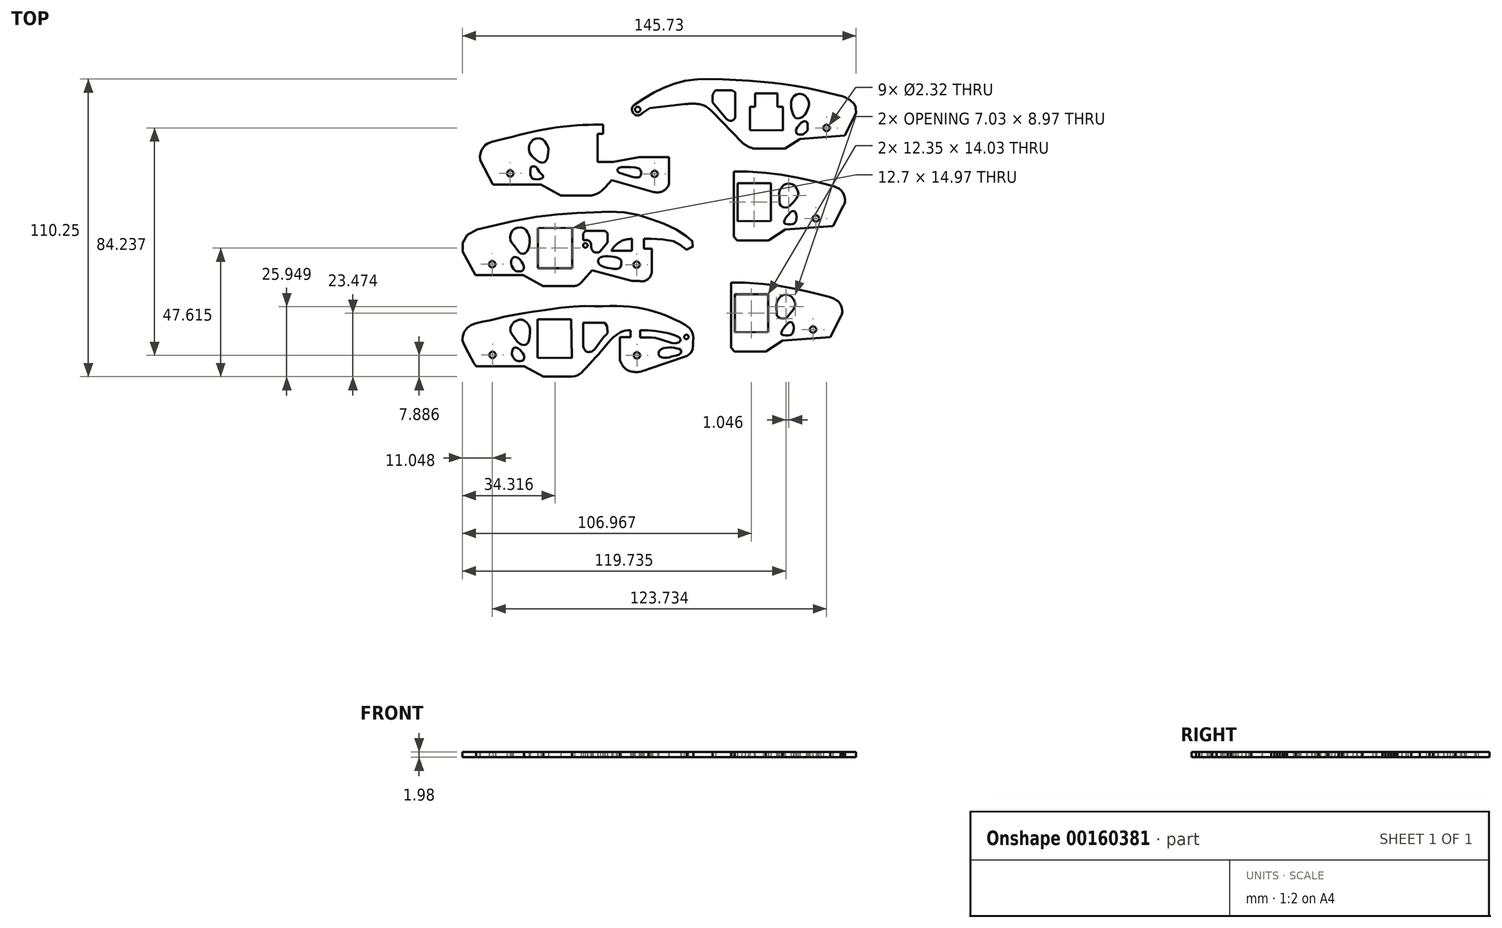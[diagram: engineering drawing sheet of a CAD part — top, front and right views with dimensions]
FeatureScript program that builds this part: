
annotation { "Feature Type Name" : "Feature", "Feature Type Description" : "" }
export const myFeature = defineFeature(function(context is Context, id is Id, definition is map)
    precondition{}
    {
        {
            var Q0;
            Q0=qCreatedBy(makeId("Top.planeOp"),FACE);
            var sketch = newSketch(context, id + "F0", { "sketchPlane" : qUnion([Q0])});
            skLineSegment(sketch, "E0", {"start": v(102.72, 106.46) * mm, "end": v(113.6, 95.26) * mm});
            skLineSegment(sketch, "E1", {"start": v(155.9, 105.94) * mm, "end": v(151.6, 97.67) * mm});
            skLineSegment(sketch, "E2", {"start": v(151.6, 97.67) * mm, "end": v(135.17, 96.41) * mm});
            skLineSegment(sketch, "E3", {"start": v(135.17, 96.41) * mm, "end": v(129.52, 92.85) * mm});
            skLineSegment(sketch, "E4", {"start": v(129.52, 92.85) * mm, "end": v(118.1, 92.85) * mm});
            skLineSegment(sketch, "E5", {"start": v(79.59, 107.92) * mm, "end": v(92.64, 109.39) * mm});
            skFitSpline(sketch, "E6", {"points": [v(76.87, 106.15) * mm, v(75.51, 105.3) * mm, v(74.14, 105.41) * mm, v(73, 106.88) * mm, v(73.1, 108.24) * mm, v(74.04, 109.29) * mm], "startDerivative": vector(-5.69, -6.58) * mm, "endDerivative": vector(5.78, 5.04) * mm});
            skPoint(sketch, "E7.10.internal.snap0", {"position": v(86.11, 108.66) * mm});
            skFitSpline(sketch, "E7", {"points": [v(74.04, 109.29) * mm, v(82.52, 114.41) * mm, v(92.64, 117.97) * mm, v(105.34, 118.6) * mm, v(118.84, 117.87) * mm, v(129.73, 116.72) * mm, v(140.61, 114.73) * mm, v(148.25, 112.84) * mm, v(152.55, 111.59) * mm, v(155.16, 109.39) * mm, v(155.57, 108.66) * mm, v(155.9, 105.94) * mm], "startDerivative": vector(74.24, 51.65) * mm, "endDerivative": vector(-2.1, -59) * mm});
            skFitSpline(sketch, "E8", {"points": [v(92.64, 109.39) * mm, v(97.7, 109.39) * mm, v(100.84, 108.13) * mm, v(102.72, 106.46) * mm], "startDerivative": vector(9.18, 0.98) * mm, "endDerivative": vector(5.58, -5.6) * mm});
            skFitSpline(sketch, "E9", {"points": [v(113.6, 95.26) * mm, v(115.5, 93.9) * mm, v(118.1, 92.85) * mm], "startDerivative": vector(3.71, -3.06) * mm, "endDerivative": vector(5.26, -1.77) * mm});
            skLineSegment(sketch, "E10", {"start": v(76.87, 106.15) * mm, "end": v(79.59, 107.92) * mm});
            skLineSegment(sketch, "E11", {"start": v(111.2, 105) * mm, "end": v(111.2, 113.68) * mm});
            skLineSegment(sketch, "E12", {"start": v(103.87, 114.52) * mm, "end": v(109.94, 114.52) * mm});
            skLineSegment(sketch, "E13", {"start": v(109.94, 114.52) * mm, "end": v(111.2, 113.68) * mm});
            skLineSegment(sketch, "E14", {"start": v(102.83, 110.02) * mm, "end": v(107.75, 104.05) * mm});
            skArc(sketch, "E15", {"start": v(107.75, 104.05) * mm, "mid": v(108.68, 103.37) * mm, "end": v(109.84, 103.21) * mm});
            skArc(sketch, "E16", {"start": v(111.2, 105) * mm, "mid": v(110.82, 103.87) * mm, "end": v(109.84, 103.21) * mm});
            skFitSpline(sketch, "E17", {"points": [v(102.83, 110.02) * mm, v(102.83, 112.74) * mm, v(103.87, 114.52) * mm], "startDerivative": vector(-0.6, 5.43) * mm, "endDerivative": vector(2.77, 3.53) * mm});
            skPoint(sketch, "E18.0.internal.snap0", {"position": v(105.29, 107.04) * mm});
            skFitSpline(sketch, "E18", {"points": [v(132.13, 107.04) * mm, v(131.82, 109.8) * mm, v(133.18, 112.64) * mm, v(136.32, 112.95) * mm, v(138, 111.17) * mm, v(138.41, 109.18) * mm, v(136.95, 105.55) * mm, v(134.65, 104.05) * mm, v(133.18, 104.47) * mm, v(132.13, 107.04) * mm]});
            skFitSpline(sketch, "E19", {"points": [v(133.8, 100.16) * mm, v(134.89, 101.65) * mm, v(135.97, 102.73) * mm, v(136.8, 103.02) * mm, v(137.84, 102.44) * mm, v(137.92, 100.9) * mm, v(137.88, 99.7) * mm, v(137.05, 98.79) * mm, v(136.26, 98.16) * mm, v(134.68, 98.12) * mm, v(134.02, 98.41) * mm, v(133.73, 98.91) * mm, v(133.8, 100.16) * mm]});
            skLineSegment(sketch, "E20", {"start": v(116.6, 99.72) * mm, "end": v(116.6, 108.38) * mm});
            skLineSegment(sketch, "E21", {"start": v(116.6, 108.38) * mm, "end": v(118.53, 108.38) * mm});
            skLineSegment(sketch, "E22", {"start": v(118.53, 108.38) * mm, "end": v(118.53, 113.41) * mm});
            skLineSegment(sketch, "E23", {"start": v(118.53, 113.41) * mm, "end": v(126.77, 113.41) * mm});
            skLineSegment(sketch, "E24", {"start": v(126.77, 113.41) * mm, "end": v(126.77, 108.42) * mm});
            skLineSegment(sketch, "E25", {"start": v(126.77, 108.42) * mm, "end": v(128.76, 108.42) * mm});
            skLineSegment(sketch, "E26", {"start": v(128.76, 108.42) * mm, "end": v(128.76, 99.68) * mm});
            skLineSegment(sketch, "E27", {"start": v(128.76, 99.68) * mm, "end": v(116.6, 99.72) * mm});
            skCircle(sketch, "E28", {"center": v(144.95, 100.53) * mm, "radius": 1.16 * mm});
            skCircle(sketch, "E29", {"center": v(75.05, 107.38) * mm, "radius": 1 * mm});
            skCircle(sketch, "E30", {"center": v(141, 67.03) * mm, "radius": 1.16 * mm});
            skLineSegment(sketch, "E31", {"start": v(110.65, 84.35) * mm, "end": v(110.65, 60.33) * mm});
            skLineSegment(sketch, "E32", {"start": v(110.65, 60.33) * mm, "end": v(111.9, 58.86) * mm});
            skLineSegment(sketch, "E33", {"start": v(111.9, 58.86) * mm, "end": v(123.52, 58.86) * mm});
            skLineSegment(sketch, "E34", {"start": v(123.52, 58.86) * mm, "end": v(129.7, 62.94) * mm});
            skLineSegment(sketch, "E35", {"start": v(129.7, 62.94) * mm, "end": v(147.39, 64.2) * mm});
            skLineSegment(sketch, "E36", {"start": v(147.39, 64.2) * mm, "end": v(151.16, 71.74) * mm});
            skLineSegment(sketch, "E37", {"start": v(112, 66.03) * mm, "end": v(112, 80.06) * mm});
            skLineSegment(sketch, "E38", {"start": v(112, 80.06) * mm, "end": v(124.36, 80.06) * mm});
            skLineSegment(sketch, "E39", {"start": v(124.36, 80.06) * mm, "end": v(124.36, 66.08) * mm});
            skLineSegment(sketch, "E40", {"start": v(124.36, 66.08) * mm, "end": v(112, 66.03) * mm});
            skLineSegment(sketch, "E41", {"start": v(115.93, 84.35) * mm, "end": v(122.58, 83.93) * mm});
            skLineSegment(sketch, "E42", {"start": v(122.58, 83.93) * mm, "end": v(128.08, 83.25) * mm});
            skLineSegment(sketch, "E43", {"start": v(128.08, 83.25) * mm, "end": v(133.62, 82.26) * mm});
            skLineSegment(sketch, "E44", {"start": v(133.62, 82.26) * mm, "end": v(138.5, 81.2) * mm});
            skLineSegment(sketch, "E45", {"start": v(138.5, 81.2) * mm, "end": v(142.73, 80.21) * mm});
            skLineSegment(sketch, "E46", {"start": v(142.73, 80.21) * mm, "end": v(147.28, 79.06) * mm});
            skLineSegment(sketch, "E47", {"start": v(110.65, 84.35) * mm, "end": v(115.93, 84.35) * mm});
            skFitSpline(sketch, "E48", {"points": [v(147.28, 79.06) * mm, v(149.48, 78.05) * mm, v(150.98, 76.64) * mm, v(151.5, 75.37) * mm, v(151.77, 74.14) * mm, v(151.68, 72.77) * mm, v(151.16, 71.74) * mm], "startDerivative": vector(11.1, -4.26) * mm, "endDerivative": vector(-4.35, -6.8) * mm});
            skFitSpline(sketch, "E49", {"points": [v(127.44, 76.2) * mm, v(127.74, 77.57) * mm, v(128.54, 78.76) * mm, v(129.6, 79.68) * mm, v(131.3, 79.99) * mm, v(133.11, 79.2) * mm, v(134.08, 77.66) * mm, v(134.48, 76.34) * mm, v(133.95, 74.75) * mm, v(131.18, 71.5) * mm, v(130.47, 71.06) * mm, v(128.84, 71.23) * mm, v(127.7, 72.07) * mm, v(127.57, 72.86) * mm, v(127.44, 76.2) * mm]});
            skFitSpline(sketch, "E50", {"points": [v(129.72, 67) * mm, v(131.3, 69.03) * mm, v(132.01, 69.65) * mm, v(132.9, 69.73) * mm, v(133.68, 68.81) * mm, v(133.73, 66.39) * mm, v(133.07, 65.25) * mm, v(132.5, 64.98) * mm, v(129.94, 64.94) * mm, v(129.24, 65.47) * mm, v(129.33, 66.08) * mm, v(129.72, 67) * mm]});
            skCircle(sketch, "E51", {"center": v(139.96, 25.86) * mm, "radius": 1.16 * mm});
            skLineSegment(sketch, "E52", {"start": v(109.6, 43.19) * mm, "end": v(109.6, 19.17) * mm});
            skLineSegment(sketch, "E53", {"start": v(109.6, 19.17) * mm, "end": v(110.86, 17.7) * mm});
            skLineSegment(sketch, "E54", {"start": v(110.86, 17.7) * mm, "end": v(122.48, 17.7) * mm});
            skLineSegment(sketch, "E55", {"start": v(122.48, 17.7) * mm, "end": v(128.65, 21.78) * mm});
            skLineSegment(sketch, "E56", {"start": v(128.65, 21.78) * mm, "end": v(146.34, 23.04) * mm});
            skLineSegment(sketch, "E57", {"start": v(146.34, 23.04) * mm, "end": v(150.1, 30.58) * mm});
            skLineSegment(sketch, "E58", {"start": v(110.96, 24.87) * mm, "end": v(110.96, 38.9) * mm});
            skLineSegment(sketch, "E59", {"start": v(110.96, 38.9) * mm, "end": v(123.31, 38.9) * mm});
            skLineSegment(sketch, "E60", {"start": v(123.31, 38.9) * mm, "end": v(123.31, 24.92) * mm});
            skLineSegment(sketch, "E61", {"start": v(123.31, 24.92) * mm, "end": v(110.96, 24.87) * mm});
            skLineSegment(sketch, "E62", {"start": v(114.89, 43.19) * mm, "end": v(121.53, 42.77) * mm});
            skLineSegment(sketch, "E63", {"start": v(121.53, 42.77) * mm, "end": v(127.03, 42.09) * mm});
            skLineSegment(sketch, "E64", {"start": v(127.03, 42.09) * mm, "end": v(132.58, 41.1) * mm});
            skLineSegment(sketch, "E65", {"start": v(132.58, 41.1) * mm, "end": v(137.44, 40.05) * mm});
            skLineSegment(sketch, "E66", {"start": v(137.44, 40.05) * mm, "end": v(141.68, 39.05) * mm});
            skLineSegment(sketch, "E67", {"start": v(141.68, 39.05) * mm, "end": v(146.24, 37.9) * mm});
            skLineSegment(sketch, "E68", {"start": v(109.6, 43.19) * mm, "end": v(114.89, 43.19) * mm});
            skFitSpline(sketch, "E69", {"points": [v(146.24, 37.9) * mm, v(148.44, 36.9) * mm, v(149.93, 35.48) * mm, v(150.46, 34.2) * mm, v(150.73, 32.98) * mm, v(150.64, 31.61) * mm, v(150.1, 30.58) * mm], "startDerivative": vector(11.1, -4.26) * mm, "endDerivative": vector(-4.35, -6.8) * mm});
            skFitSpline(sketch, "E70", {"points": [v(126.39, 35.04) * mm, v(126.7, 36.4) * mm, v(127.49, 37.6) * mm, v(128.55, 38.52) * mm, v(130.26, 38.83) * mm, v(132.07, 38.04) * mm, v(133.03, 36.5) * mm, v(133.43, 35.18) * mm, v(132.9, 33.6) * mm, v(130.13, 30.33) * mm, v(129.43, 29.9) * mm, v(127.8, 30.07) * mm, v(126.65, 30.9) * mm, v(126.52, 31.7) * mm, v(126.39, 35.04) * mm]});
            skFitSpline(sketch, "E71", {"points": [v(128.68, 25.85) * mm, v(130.26, 27.87) * mm, v(130.97, 28.49) * mm, v(131.85, 28.57) * mm, v(132.64, 27.65) * mm, v(132.68, 25.23) * mm, v(132.02, 24.09) * mm, v(131.45, 23.82) * mm, v(128.9, 23.78) * mm, v(128.2, 24.3) * mm, v(128.28, 24.92) * mm, v(128.68, 25.85) * mm]});
            skCircle(sketch, "E72", {"center": v(21.22, 50.05) * mm, "radius": 1.16 * mm});
            skCircle(sketch, "E73", {"center": v(74.64, 49.88) * mm, "radius": 1.16 * mm});
            skCircle(sketch, "E74", {"center": v(55.7, 57.03) * mm, "radius": 0.83 * mm});
            skLineSegment(sketch, "E75", {"start": v(10.25, 54.7) * mm, "end": v(15.07, 46.06) * mm});
            skLineSegment(sketch, "E76", {"start": v(15.07, 46.06) * mm, "end": v(32.68, 46.06) * mm});
            skLineSegment(sketch, "E77", {"start": v(32.68, 46.06) * mm, "end": v(40.08, 41.99) * mm});
            skLineSegment(sketch, "E78", {"start": v(40.08, 41.99) * mm, "end": v(51.7, 41.99) * mm});
            skLineSegment(sketch, "E79", {"start": v(54.12, 43.24) * mm, "end": v(58.19, 47.8) * mm});
            skLineSegment(sketch, "E80", {"start": v(58.19, 47.8) * mm, "end": v(72.98, 43.82) * mm});
            skLineSegment(sketch, "E81", {"start": v(80.29, 46.97) * mm, "end": v(80.29, 55.8) * mm});
            skLineSegment(sketch, "E82", {"start": v(80.29, 55.8) * mm, "end": v(77.38, 55.8) * mm});
            skLineSegment(sketch, "E83", {"start": v(77.38, 55.8) * mm, "end": v(77.38, 59.52) * mm});
            skLineSegment(sketch, "E84", {"start": v(77.38, 59.52) * mm, "end": v(79.96, 59.52) * mm});
            skLineSegment(sketch, "E85", {"start": v(38.14, 63.46) * mm, "end": v(38.14, 48.54) * mm});
            skLineSegment(sketch, "E86", {"start": v(38.14, 48.54) * mm, "end": v(50.84, 48.54) * mm});
            skLineSegment(sketch, "E87", {"start": v(50.84, 48.54) * mm, "end": v(50.84, 63.51) * mm});
            skLineSegment(sketch, "E88", {"start": v(50.84, 63.51) * mm, "end": v(38.14, 63.46) * mm});
            skLineSegment(sketch, "E89", {"start": v(54.94, 59.02) * mm, "end": v(54.94, 61.46) * mm});
            skLineSegment(sketch, "E90", {"start": v(54.94, 61.46) * mm, "end": v(55.66, 62.46) * mm});
            skLineSegment(sketch, "E91", {"start": v(55.66, 62.46) * mm, "end": v(62.98, 62.46) * mm});
            skLineSegment(sketch, "E92", {"start": v(62.98, 62.46) * mm, "end": v(63.92, 61.51) * mm});
            skLineSegment(sketch, "E93", {"start": v(63.92, 61.51) * mm, "end": v(63.92, 58.08) * mm});
            skLineSegment(sketch, "E94", {"start": v(63.92, 58.08) * mm, "end": v(61.26, 54.92) * mm});
            skLineSegment(sketch, "E95", {"start": v(54.94, 59.02) * mm, "end": v(56.38, 59.02) * mm});
            skLineSegment(sketch, "E96", {"start": v(67.08, 55.03) * mm, "end": v(72.96, 55.03) * mm});
            skLineSegment(sketch, "E97", {"start": v(72.96, 55.03) * mm, "end": v(72.96, 59.46) * mm});
            skLineSegment(sketch, "E98", {"start": v(72.96, 59.46) * mm, "end": v(72.68, 59.46) * mm});
            skFitSpline(sketch, "E99", {"points": [v(10.25, 54.7) * mm, v(10.25, 57.4) * mm, v(11.2, 59.92) * mm, v(13.64, 62.06) * mm, v(20.45, 64.06) * mm, v(35.99, 67.4) * mm, v(50.27, 68.95) * mm, v(60.27, 69.4) * mm, v(68.04, 69.4) * mm, v(75.22, 68.35) * mm, v(80.84, 66.5) * mm, v(86.54, 64.36) * mm, v(91.72, 61.47) * mm, v(94.24, 59.62) * mm, v(95.35, 58.44) * mm, v(95.65, 57.4) * mm, v(95.13, 56.14) * mm, v(93.57, 55.4) * mm, v(91.95, 56.22) * mm, v(90.17, 57.77) * mm, v(88.32, 58.58) * mm, v(84.62, 59.25) * mm, v(79.96, 59.52) * mm], "startDerivative": vector(-5.32, 76.94) * mm, "endDerivative": vector(-101.27, 3.31) * mm});
            skFitSpline(sketch, "E100", {"points": [v(72.98, 43.82) * mm, v(75.66, 43.82) * mm, v(77.51, 43.82) * mm, v(79.51, 45.19) * mm, v(80.29, 46.97) * mm], "startDerivative": vector(10.28, 0.34) * mm, "endDerivative": vector(2.21, 7.85) * mm});
            skFitSpline(sketch, "E101", {"points": [v(31.1, 54.59) * mm, v(29.28, 57) * mm, v(28.1, 58.59) * mm, v(27.9, 60.22) * mm, v(28.54, 62.3) * mm, v(29.92, 63.43) * mm, v(31.65, 63.68) * mm, v(33.33, 63.18) * mm, v(34.37, 61.75) * mm, v(34.96, 60.12) * mm, v(35, 57.85) * mm, v(34.51, 55.53) * mm, v(33.72, 54.4) * mm, v(32.98, 54.04) * mm, v(32, 53.95) * mm, v(31.1, 54.59) * mm]});
            skFitSpline(sketch, "E102", {"points": [v(28.2, 50.34) * mm, v(28.34, 51.67) * mm, v(28.83, 52.41) * mm, v(29.57, 52.76) * mm, v(30.76, 52.41) * mm, v(32.14, 50.88) * mm, v(32.78, 49.75) * mm, v(32.93, 48.7) * mm, v(32.44, 47.67) * mm, v(31.65, 47.43) * mm, v(30.36, 47.43) * mm, v(29.57, 47.82) * mm, v(28.63, 49.06) * mm, v(28.2, 50.34) * mm]});
            skFitSpline(sketch, "E103", {"points": [v(56.38, 59.02) * mm, v(57.27, 58.55) * mm, v(57.8, 57.5) * mm, v(57.84, 56.52) * mm, v(58.06, 55.6) * mm, v(58.59, 54.8) * mm, v(59.55, 54.41) * mm, v(60.65, 54.5) * mm, v(61.26, 54.92) * mm], "startDerivative": vector(7.58, -2.73) * mm, "endDerivative": vector(4.95, 4.46) * mm});
            skFitSpline(sketch, "E104", {"points": [v(67.08, 55.03) * mm, v(65.9, 55.03) * mm, v(65.5, 55.03) * mm, v(65.98, 56.17) * mm, v(67.08, 57.23) * mm, v(68.53, 58.37) * mm, v(70.2, 59.12) * mm, v(72.68, 59.46) * mm], "startDerivative": vector(-9.88, 0.58) * mm, "endDerivative": vector(13.82, 1.22) * mm});
            skFitSpline(sketch, "E105", {"points": [v(60.4, 51.42) * mm, v(61.05, 52.39) * mm, v(62.33, 52.96) * mm, v(64.7, 52.96) * mm, v(67.34, 52.6) * mm, v(68.88, 51.6) * mm, v(69.02, 50.58) * mm, v(68.75, 49.04) * mm, v(67.6, 48.34) * mm, v(64.8, 48.56) * mm, v(61.93, 49.3) * mm, v(60.65, 50.32) * mm, v(60.4, 51.42) * mm]});
            skFitSpline(sketch, "E106", {"points": [v(51.7, 41.99) * mm, v(53.04, 42.4) * mm, v(54.12, 43.24) * mm], "startDerivative": vector(2.77, 0.58) * mm, "endDerivative": vector(2.05, 1.92) * mm});
            skCircle(sketch, "E107", {"center": v(21.34, 16.46) * mm, "radius": 1.16 * mm});
            skCircle(sketch, "E108", {"center": v(74.76, 16.3) * mm, "radius": 1.16 * mm});
            skCircle(sketch, "E109", {"center": v(93.09, 23.12) * mm, "radius": 0.81 * mm});
            skLineSegment(sketch, "E110", {"start": v(72.44, 25.54) * mm, "end": v(72.44, 23.02) * mm});
            skLineSegment(sketch, "E111", {"start": v(72.44, 23.02) * mm, "end": v(68.49, 23.02) * mm});
            skLineSegment(sketch, "E112", {"start": v(68.49, 23.02) * mm, "end": v(68.49, 14.57) * mm});
            skLineSegment(sketch, "E113", {"start": v(79.06, 11.27) * mm, "end": v(93.24, 16.1) * mm});
            skFitSpline(sketch, "E114", {"points": [v(68.49, 14.57) * mm, v(69.38, 12.65) * mm, v(71.15, 10.92) * mm, v(72.98, 10.28) * mm, v(75.45, 10.18) * mm, v(79.06, 11.27) * mm], "startDerivative": vector(3.86, -10.63) * mm, "endDerivative": vector(15.26, 5.73) * mm});
            skFitSpline(sketch, "E115", {"points": [v(93.24, 16.1) * mm, v(94.52, 16.95) * mm, v(95.36, 18.58) * mm, v(95.5, 20.8) * mm, v(95.6, 23.17) * mm, v(94.96, 25.44) * mm, v(91.8, 28.06) * mm, v(84.05, 31.57) * mm, v(76.93, 33.6) * mm, v(70.26, 34.48) * mm, v(62.15, 34.54) * mm], "startDerivative": vector(22.58, 11.43) * mm, "endDerivative": vector(-62.19, -2.42) * mm});
            skLineSegment(sketch, "E116", {"start": v(75.95, 25.6) * mm, "end": v(75.95, 22.97) * mm});
            skLineSegment(sketch, "E117", {"start": v(75.95, 22.97) * mm, "end": v(80.2, 22.97) * mm});
            skFitSpline(sketch, "E118", {"points": [v(75.95, 25.6) * mm, v(79.35, 25.6) * mm, v(82.81, 25.15) * mm, v(86.76, 24.36) * mm, v(89.18, 23.57) * mm, v(90.67, 22.78) * mm, v(90.96, 22.08) * mm, v(90.62, 21.4) * mm, v(89.68, 20.95) * mm, v(88.34, 20.85) * mm, v(85.87, 21.44) * mm, v(83.26, 22.28) * mm, v(80.2, 22.97) * mm], "startDerivative": vector(32.68, 0.95) * mm, "endDerivative": vector(-30.84, 1.47) * mm});
            skFitSpline(sketch, "E119", {"points": [v(82.91, 17.88) * mm, v(84.4, 18.87) * mm, v(86.27, 19.22) * mm, v(87.65, 19.22) * mm, v(89.48, 18.92) * mm, v(90.52, 18.63) * mm, v(91.11, 18.03) * mm, v(91.11, 17.3) * mm, v(90.47, 16.65) * mm, v(87.7, 15.86) * mm, v(86.22, 15.46) * mm, v(85.48, 15.37) * mm, v(84.44, 15.51) * mm, v(83.65, 15.71) * mm, v(82.96, 16.3) * mm, v(82.81, 17) * mm, v(82.91, 17.88) * mm]});
            skFitSpline(sketch, "E120", {"points": [v(62.15, 34.54) * mm, v(53.7, 34.54) * mm, v(40.85, 33.14) * mm, v(34.35, 32.17) * mm, v(25.55, 30.56) * mm, v(20.3, 29.3) * mm, v(14.93, 28.11) * mm, v(12.98, 27.28) * mm, v(11.3, 25.74) * mm, v(10.39, 23.85) * mm, v(10.18, 22.04) * mm, v(10.67, 20.57) * mm, v(14.95, 12.6) * mm, v(15.28, 12.24) * mm], "startDerivative": vector(-67.55, -3.97) * mm, "endDerivative": vector(4.14, 19.83) * mm});
            skLineSegment(sketch, "E121", {"start": v(15.28, 12.24) * mm, "end": v(33.1, 12.24) * mm});
            skLineSegment(sketch, "E122", {"start": v(33.1, 12.24) * mm, "end": v(40.15, 8.41) * mm});
            skLineSegment(sketch, "E123", {"start": v(40.15, 8.41) * mm, "end": v(50.77, 8.41) * mm});
            skFitSpline(sketch, "E124", {"points": [v(50.77, 8.41) * mm, v(52.93, 8.97) * mm, v(54.82, 10.5) * mm, v(59.15, 15.12) * mm, v(62.78, 19.38) * mm, v(65.79, 22.74) * mm, v(68.1, 24.48) * mm, v(69.98, 25.39) * mm, v(72.44, 25.54) * mm], "startDerivative": vector(22.81, 3.88) * mm, "endDerivative": vector(25.16, -3.8) * mm});
            skFitSpline(sketch, "E125", {"points": [v(31.34, 20.64) * mm, v(29.8, 22.32) * mm, v(28.62, 23.92) * mm, v(27.92, 25.88) * mm, v(28.9, 28.25) * mm, v(30.58, 29.3) * mm, v(32.32, 29.51) * mm, v(33.72, 28.67) * mm, v(35.05, 26.79) * mm, v(35.12, 23.5) * mm, v(34.42, 20.92) * mm, v(33.51, 20.15) * mm, v(32.46, 20.15) * mm, v(31.34, 20.64) * mm]});
            skFitSpline(sketch, "E126", {"points": [v(28.62, 16.3) * mm, v(28.62, 17.98) * mm, v(29.18, 19.03) * mm, v(30.44, 19.1) * mm, v(32.6, 17) * mm, v(33.02, 15.82) * mm, v(32.88, 14.77) * mm, v(32.04, 14.21) * mm, v(30.79, 14.21) * mm, v(29.95, 14.5) * mm, v(28.62, 16.3) * mm]});
            skLineSegment(sketch, "E127", {"start": v(37.99, 15.42) * mm, "end": v(37.99, 29.67) * mm});
            skLineSegment(sketch, "E128", {"start": v(37.99, 29.67) * mm, "end": v(50.4, 29.67) * mm});
            skLineSegment(sketch, "E129", {"start": v(50.4, 29.67) * mm, "end": v(50.7, 15.34) * mm});
            skLineSegment(sketch, "E130", {"start": v(50.7, 15.34) * mm, "end": v(37.99, 15.42) * mm});
            skLineSegment(sketch, "E131", {"start": v(63.87, 24.52) * mm, "end": v(63.82, 26.97) * mm});
            skLineSegment(sketch, "E132", {"start": v(63.82, 26.97) * mm, "end": v(62.87, 28.43) * mm});
            skLineSegment(sketch, "E133", {"start": v(62.87, 28.43) * mm, "end": v(54.9, 28.43) * mm});
            skLineSegment(sketch, "E134", {"start": v(54.9, 28.43) * mm, "end": v(54.9, 19.66) * mm});
            skFitSpline(sketch, "E135", {"points": [v(54.9, 19.66) * mm, v(55.23, 18.75) * mm, v(56.14, 17.67) * mm, v(57.14, 17.54) * mm, v(58.3, 17.87) * mm, v(60.8, 20.82) * mm, v(62.5, 23.03) * mm, v(63.87, 24.52) * mm], "startDerivative": vector(2.3, -8.2) * mm, "endDerivative": vector(9.03, 9.5) * mm});
            skLineSegment(sketch, "E136", {"start": v(16.78, 88.57) * mm, "end": v(21.45, 79.56) * mm});
            skLineSegment(sketch, "E137", {"start": v(21.45, 79.56) * mm, "end": v(39.3, 79.56) * mm});
            skLineSegment(sketch, "E138", {"start": v(39.3, 79.56) * mm, "end": v(46.6, 75.46) * mm});
            skLineSegment(sketch, "E139", {"start": v(46.6, 75.46) * mm, "end": v(57.98, 75.46) * mm});
            skLineSegment(sketch, "E140", {"start": v(58.55, 101.75) * mm, "end": v(62.23, 101.75) * mm});
            skLineSegment(sketch, "E141", {"start": v(62.23, 101.75) * mm, "end": v(62.23, 98.32) * mm});
            skLineSegment(sketch, "E142", {"start": v(62.23, 98.32) * mm, "end": v(60.27, 98.32) * mm});
            skLineSegment(sketch, "E143", {"start": v(60.27, 98.32) * mm, "end": v(60.27, 87.89) * mm});
            skLineSegment(sketch, "E144", {"start": v(60.27, 87.89) * mm, "end": v(65.98, 87.89) * mm});
            skLineSegment(sketch, "E145", {"start": v(65.97, 87.89) * mm, "end": v(75.55, 89.79) * mm});
            skLineSegment(sketch, "E146", {"start": v(65.48, 81.26) * mm, "end": v(80.58, 76.85) * mm});
            skLineSegment(sketch, "E147", {"start": v(44.84, 90.86) * mm, "end": v(47.44, 90.86) * mm});
            skLineSegment(sketch, "E148", {"start": v(47.44, 90.86) * mm, "end": v(47.44, 96.9) * mm});
            skLineSegment(sketch, "E149", {"start": v(47.4, 96.9) * mm, "end": v(55.73, 96.9) * mm});
            skLineSegment(sketch, "E150", {"start": v(55.73, 96.9) * mm, "end": v(55.73, 90.78) * mm});
            skLineSegment(sketch, "E151", {"start": v(55.82, 90.78) * mm, "end": v(57.77, 90.78) * mm});
            skLineSegment(sketch, "E152", {"start": v(57.77, 90.86) * mm, "end": v(57.77, 82.62) * mm});
            skLineSegment(sketch, "E153", {"start": v(57.81, 82.26) * mm, "end": v(44.97, 82.26) * mm});
            skLineSegment(sketch, "E154", {"start": v(44.97, 82.66) * mm, "end": v(44.84, 90.86) * mm});
            skFitSpline(sketch, "E155", {"points": [v(16.78, 88.57) * mm, v(16.78, 90.96) * mm, v(17.36, 92.52) * mm, v(18.23, 93.8) * mm, v(19.5, 94.78) * mm, v(24.49, 96.23) * mm, v(33.64, 98.55) * mm, v(40.07, 99.94) * mm, v(46.5, 100.92) * mm, v(54.02, 101.61) * mm, v(58.55, 101.75) * mm], "startDerivative": vector(-2.79, 34.04) * mm, "endDerivative": vector(40.85, 0.58) * mm});
            skFitSpline(sketch, "E156", {"points": [v(57.98, 75.46) * mm, v(60.97, 76.71) * mm, v(63.06, 78.57) * mm, v(65.48, 81.26) * mm], "startDerivative": vector(9.6, 2.92) * mm, "endDerivative": vector(7.03, 7.9) * mm});
            skFitSpline(sketch, "E157", {"points": [v(38.62, 87.95) * mm, v(36.65, 89.45) * mm, v(35.32, 90.9) * mm, v(34.8, 92.58) * mm, v(34.91, 94.14) * mm, v(35.78, 95.65) * mm, v(36.82, 96.46) * mm, v(39.31, 96.63) * mm, v(40.7, 95.48) * mm, v(41.63, 94.09) * mm, v(42.03, 92.64) * mm, v(41.8, 90.79) * mm, v(41.4, 88.76) * mm, v(40.76, 88) * mm, v(40.12, 87.77) * mm, v(38.62, 87.95) * mm]});
            skFitSpline(sketch, "E158", {"points": [v(35.37, 83.26) * mm, v(35.32, 85.17) * mm, v(35.72, 86.15) * mm, v(36.7, 86.33) * mm, v(37.7, 85.8) * mm, v(38.39, 84.59) * mm, v(39.26, 83.66) * mm, v(39.95, 83.02) * mm, v(39.95, 82.9) * mm, v(39.95, 82.16) * mm, v(38.68, 81.58) * mm, v(36.42, 81.63) * mm, v(35.72, 82.16) * mm, v(35.37, 83.26) * mm]});
            skFitSpline(sketch, "E159", {"points": [v(67.92, 85.69) * mm, v(74.53, 85.86) * mm, v(75.92, 85.16) * mm, v(76.44, 83.95) * mm, v(76.1, 82.85) * mm, v(75.34, 82.27) * mm, v(74, 82.27) * mm, v(69.84, 83.43) * mm, v(67.87, 84.18) * mm, v(67.58, 84.88) * mm, v(67.92, 85.69) * mm]});
            skCircle(sketch, "E160", {"center": v(27.88, 83.7) * mm, "radius": 1.16 * mm});
            skCircle(sketch, "E161", {"center": v(81.3, 83.53) * mm, "radius": 1.16 * mm});
            skLineSegment(sketch, "E162", {"start": v(86.62, 89.73) * mm, "end": v(86.62, 80.92) * mm});
            skFitSpline(sketch, "E163", {"points": [v(86.62, 80.92) * mm, v(86.62, 79.76) * mm, v(85.92, 78.43) * mm, v(85.37, 77.8) * mm, v(84.73, 77.35) * mm, v(83.68, 76.88) * mm, v(82.07, 76.66) * mm, v(80.58, 76.85) * mm], "startDerivative": vector(1, -7.4) * mm, "endDerivative": vector(-9.1, 1.74) * mm});
            skLineSegment(sketch, "E164", {"start": v(75.55, 89.79) * mm, "end": v(86.62, 89.73) * mm});
            skSolve(sketch);
        }
        {
            var Q0;
            Q0 = qSketchRegion(id + "F0", true);
            var Q1;
            Q1=sQuery(id+"F0.wireOp",EDGE,"61ec7bf3-dbb5-4754-9197-ded7b2c74904");
            var Q2;
            Q2=sQuery(id+"F0.wireOp",EDGE,"12f948d3-a610-4f78-8b6c-5a076e0a1dff");
            var Q3;
            Q3=sQuery(id+"F0.wireOp",EDGE,"43d4c9f4-bb33-4e5a-8e3e-e27920b19029");
            var Q4;
            Q4=sQuery(id+"F0.wireOp",EDGE,"32888984-c8a8-4f13-a2ea-3b4797feea4c");
            var Q5;
            Q5=sQuery(id+"F0.wireOp",EDGE,"10468318-1ef5-4b82-923f-de2a100db941");
            var Q6;
            Q6=sQuery(id+"F0.wireOp",EDGE,"3c0b0582-771c-4330-95ec-dd069cad5082");
            var Q7;
            Q7=sQuery(id+"F0.wireOp",EDGE,"672d26fe-18bd-40d7-81d1-668574ab8dfd");
            var Q8;
            Q8=sQuery(id+"F0.wireOp",EDGE,"d6da3af9-6a6e-4f10-a9ae-2975620c58e0");
            var Q9;
            Q9=sQuery(id+"F0.wireOp",EDGE,"3db5df98-4167-45b5-9579-e6855b78731f");
            var Q10;
            Q10=sQuery(id+"F0.wireOp",EDGE,"1197c900-68d8-48ef-aeb8-77163bdc8194");
            var Q11;
            Q11=sQuery(id+"F0.wireOp",EDGE,"2957fce6-174a-4bc2-908b-47fc628edd59");
            var Q12;
            Q12=sQuery(id+"F0.wireOp",EDGE,"665dce02-9dbf-43ac-80e3-72ac0c06533f");
            var Q13;
            Q13=sQuery(id+"F0.wireOp",EDGE,"d7898570-6979-41ea-94fb-ba10daed0169");
            var Q14;
            Q14=sQuery(id+"F0.wireOp",EDGE,"c454b2e1-b871-4659-97cf-96f81530cb19");
            var Q15;
            Q15=sQuery(id+"F0.wireOp",EDGE,"53d441c9-acff-4c4b-b96a-3638420ee8c7");
            var Q16;
            Q16=sQuery(id+"F0.wireOp",EDGE,"08dd1f02-a4ae-4f2a-897b-05111bd2c55c");
            var Q17;
            Q17=sQuery(id+"F0.wireOp",EDGE,"cf954042-36d8-40c7-b083-9643035ee0ab");
            var Q18;
            Q18=sQuery(id+"F0.wireOp",EDGE,"09518c72-569c-4d64-9f99-e0b228375888");
            var Q19;
            Q19=sQuery(id+"F0.wireOp",EDGE,"73751a57-68fe-4ea7-8997-5f2a3e534948");
            var Q20;
            Q20=sQuery(id+"F0.wireOp",EDGE,"abbdffda-ee5e-4ca3-9749-9f83c6a81223");
            var Q21;
            Q21=sQuery(id+"F0.wireOp",EDGE,"31f5e248-b88c-4b78-b99a-33944d0b2d93");
            var Q22;
            Q22=sQuery(id+"F0.wireOp",EDGE,"de5edd7d-ac97-45db-bfcf-3eeccb418494");
            var Q23;
            Q23=sQuery(id+"F0.wireOp",EDGE,"ad0d3cce-3bb6-4261-af79-cb62c79b08a2");
            var Q24;
            Q24=sQuery(id+"F0.wireOp",EDGE,"88d7804c-a56c-49bd-b89d-ba6a2d8b9088");
            var Q25;
            Q25=sQuery(id+"F0.wireOp",EDGE,"42321b59-9f75-4a4e-8bbf-501dac20f057");
            var Q26;
            Q26=sQuery(id+"F0.wireOp",EDGE,"95539ebf-c60e-4d8a-98ce-0e4b25c3817d");
            var Q27;
            Q27=sQuery(id+"F0.wireOp",EDGE,"0711b010-436b-4b6c-9e17-e046a1f4993f");
            var Q28;
            Q28=sQuery(id+"F0.wireOp",EDGE,"6e0bb774-3da2-4a0e-94dd-6b99b42f5add");
            var Q29;
            Q29=sQuery(id+"F0.wireOp",EDGE,"4f4537c0-825b-444a-af4b-82641a814035");
            var Q30;
            Q30=sQuery(id+"F0.wireOp",EDGE,"abc84b4c-8fab-4bae-88f2-e0f102309f46");
            var Q31;
            Q31=sQuery(id+"F0.wireOp",EDGE,"40ad693d-773d-4184-959d-caf0f4ffca3e");
            extrude(context, id + "F1", {"entities" : qUnion([Q0]), "surfaceEntities" : qUnion([Q1, Q2, Q3, Q4, Q5, Q6, Q7, Q8, Q9, Q10, Q11, Q12, Q13, Q14, Q15, Q16, Q17, Q18, Q19, Q20, Q21, Q22, Q23, Q24, Q25, Q26, Q27, Q28, Q29, Q30, Q31]), "depth" : 1.98 * mm});
        }
    });
